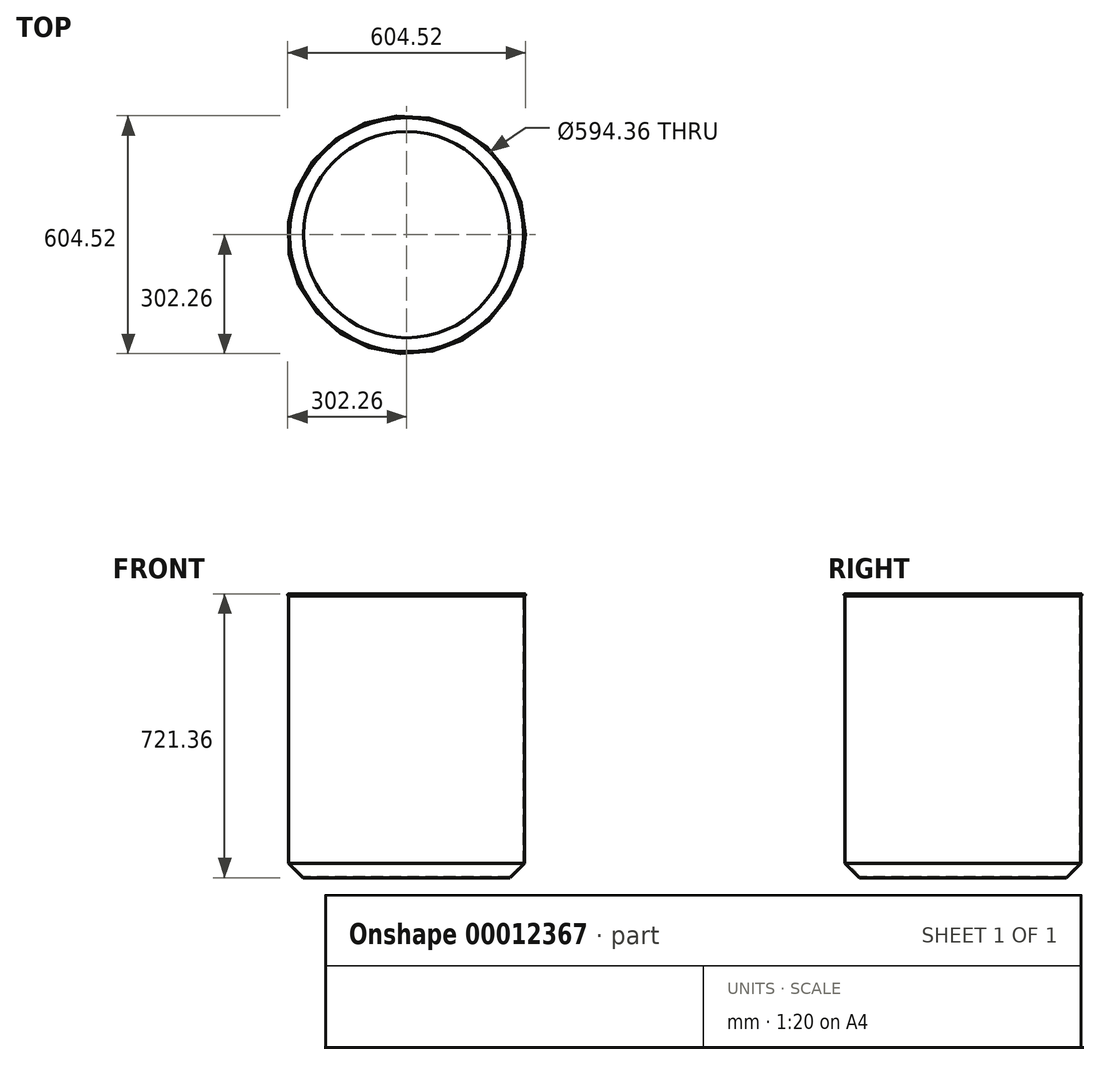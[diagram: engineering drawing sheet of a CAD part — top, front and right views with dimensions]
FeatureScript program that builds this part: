
annotation { "Feature Type Name" : "Feature", "Feature Type Description" : "" }
export const myFeature = defineFeature(function(context is Context, id is Id, definition is map)
    precondition{}
    {
        {
            var Q0;
            Q0=qCreatedBy(makeId("Right.planeOp"),FACE);
            var sketch = newSketch(context, id + "F0", { "sketchPlane" : qUnion([Q0])});
            skLineSegment(sketch, "E0", {"start": v(-299.72, 718.82) * mm, "end": v(-299.72, 36.83) * mm});
            skLineSegment(sketch, "E1", {"start": v(-299.72, 36.83) * mm, "end": v(-262.89, 0) * mm});
            skLineSegment(sketch, "E2", {"start": v(-262.9, 0) * mm, "end": v(0, 0) * mm});
            skLineSegment(sketch, "E3.0.MirrorCS", {"start": v(299.72, 718.82) * mm, "end": v(299.72, 36.83) * mm, "construction": true});
            skLineSegment(sketch, "E4.0.MirrorCS", {"start": v(299.72, 36.83) * mm, "end": v(262.89, 0) * mm, "construction": true});
            skLineSegment(sketch, "E5.0.MirrorCS", {"start": v(262.9, 0) * mm, "end": v(0, 0) * mm, "construction": true});
            skLineSegment(sketch, "E6.0", {"start": v(297.18, 718.82) * mm, "end": v(297.18, 37.88) * mm, "construction": true});
            skLineSegment(sketch, "E6.1", {"start": v(297.18, 37.88) * mm, "end": v(261.84, 2.54) * mm, "construction": true});
            skLineSegment(sketch, "E6.2", {"start": v(261.84, 2.54) * mm, "end": v(0, 2.54) * mm, "construction": true});
            skLineSegment(sketch, "E6.3", {"start": v(-261.84, 2.54) * mm, "end": v(0, 2.54) * mm});
            skLineSegment(sketch, "E6.4", {"start": v(-297.18, 37.88) * mm, "end": v(-261.84, 2.54) * mm});
            skLineSegment(sketch, "E6.5", {"start": v(-297.18, 718.82) * mm, "end": v(-297.18, 37.88) * mm});
            skLineSegment(sketch, "E7", {"start": v(-299.72, 718.82) * mm, "end": v(-297.18, 718.82) * mm});
            skLineSegment(sketch, "E8", {"start": v(299.72, 718.82) * mm, "end": v(297.18, 718.82) * mm, "construction": true});
            skLineSegment(sketch, "E9", {"start": v(0, 65.46) * mm, "end": v(0, -65.75) * mm, "construction": true});
            skLineSegment(sketch, "E10", {"start": v(0, 0) * mm, "end": v(0, 2.54) * mm});
            skCircle(sketch, "E11", {"center": v(-299.72, 718.82) * mm, "radius": 2.54 * mm});
            skSolve(sketch);
        }
        {
            var Q0;
            Q0=makeQuery(id+"F0.imprint","IMPRINT",FACE,{"disambiguationData":[TD([[makeQuery(id+"F0.imprint","IMPRINT",EDGE,{"derivedFrom":sQuery(id+"F0.wireOp",EDGE,"E0")}),1.0]])]});
            var Q1;
            {var subQ3=sQuery(id+"F0.wireOp",EDGE,"E7");Q1=makeQuery(id+"F0.imprint","IMPRINT",FACE,{"disambiguationData":[TD([[makeQuery(id+"F0.imprint","IMPRINT",EDGE,{"derivedFrom":subQ3}),1.0]])]});}
            var Q2;
            {var subQ4=sQuery(id+"F0.wireOp",EDGE,"E1");Q2=makeQuery(id+"F0.imprint","IMPRINT",FACE,{"disambiguationData":[TD([[makeQuery(id+"F0.imprint","IMPRINT",EDGE,{"derivedFrom":subQ4}),1.0]])]});}
            var Q3;
            Q3=sQuery(id+"F0.wireOp",EDGE,"E9");
            revolve(context, id + "F1", {"entities" : qUnion([Q0, Q1, Q2]), "axis" : qUnion([Q3]), "revolveType" : RevolveType.FULL});
        }
    });
